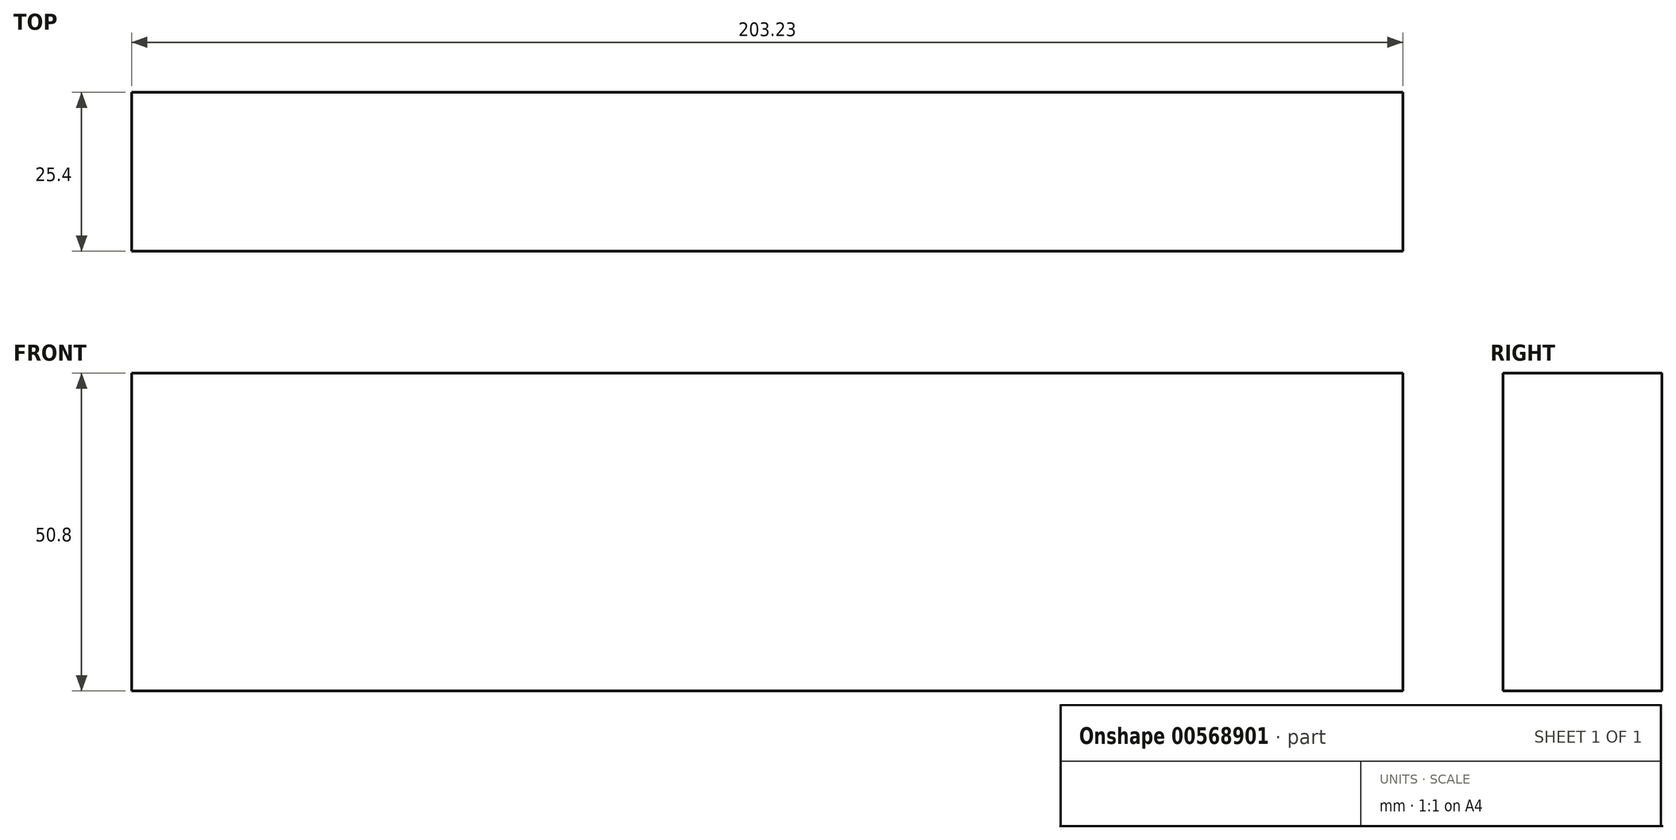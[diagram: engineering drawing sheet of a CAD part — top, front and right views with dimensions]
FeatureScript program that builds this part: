
annotation { "Feature Type Name" : "Feature", "Feature Type Description" : "" }
export const myFeature = defineFeature(function(context is Context, id is Id, definition is map)
    precondition{}
    {
        {
            var Q0;
            Q0=qCreatedBy(makeId("Front.planeOp"),FACE);
            var sketch = newSketch(context, id + "F0", { "sketchPlane" : qUnion([Q0])});
            skLineSegment(sketch, "E0", {"start": v(-96.65, -35.62) * mm, "end": v(106.58, -35.62) * mm});
            skLineSegment(sketch, "E1", {"start": v(106.58, -35.62) * mm, "end": v(106.58, 15.18) * mm});
            skLineSegment(sketch, "E2", {"start": v(106.58, 15.18) * mm, "end": v(-96.65, 15.18) * mm});
            skLineSegment(sketch, "E3", {"start": v(-96.65, 15.18) * mm, "end": v(-96.65, -35.62) * mm});
            skSolve(sketch);
        }
        {
            var Q0;
            Q0=makeQuery(id+"F0.imprint","IMPRINT",FACE,{"disambiguationData":[TD([[makeQuery(id+"F0.imprint","IMPRINT",EDGE,{"derivedFrom":sQuery(id+"F0.wireOp",EDGE,"E0")}),1.0]])]});
            extrude(context, id + "F1", {"entities" : qUnion([Q0]), "depth" : 25.4 * mm, "offsetDistance" : 25.4 * mm});
        }
    });
